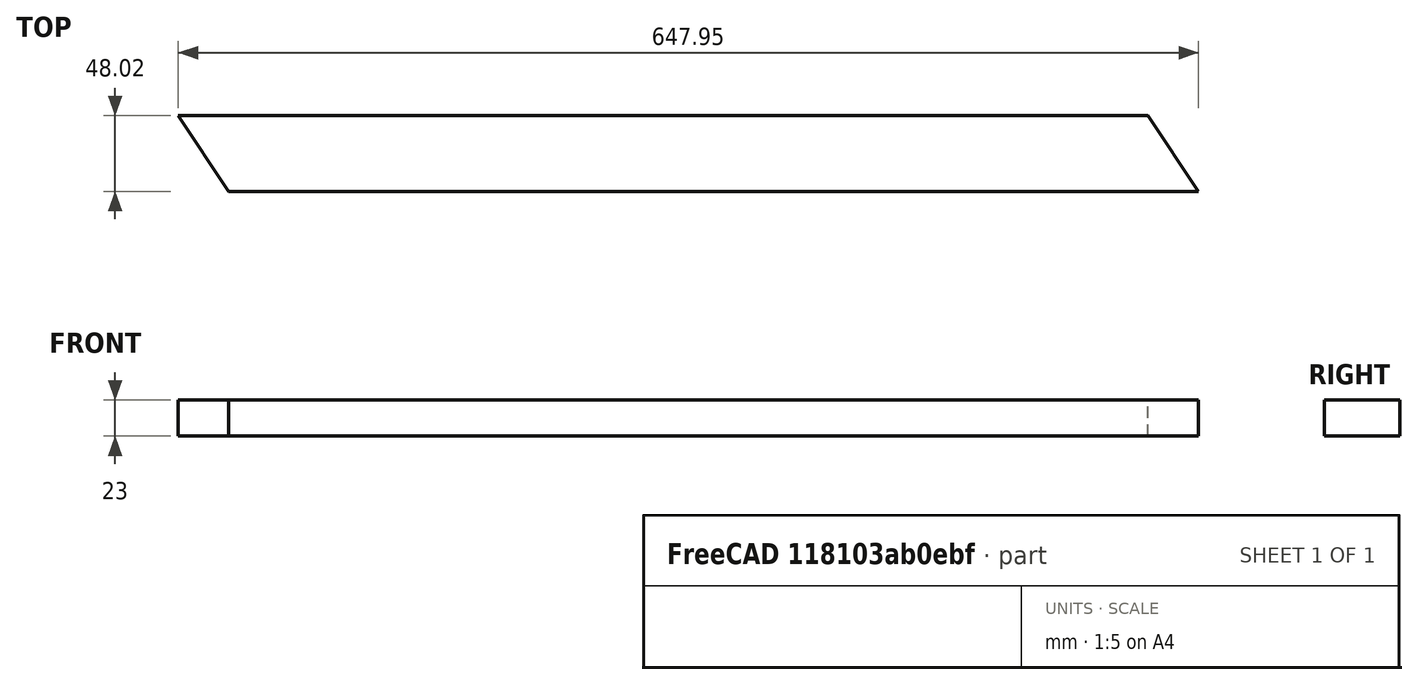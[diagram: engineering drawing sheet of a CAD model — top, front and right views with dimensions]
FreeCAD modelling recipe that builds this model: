
FCSTD DOCUMENT  (FreeCAD 0.19R24267 (Git))
Label: shelfZ
License: Creative Commons Attribution-ShareAlike
LicenseURL: http://creativecommons.org/licenses/by-sa/4.0/
objects: Sketcher::SketchObject×1, Part::Extrusion×1
note: 2 computed .brp shape members not serialized (recipe doc carries the construction recipe); baked Part::Feature solids carry a one-line shape summary decoded from their .brp
EXTERNAL_REF file=Main.FCStd obj=Spreadsheet

FEATURE [Sketcher::SketchObject] Sketch
  FullyConstrained = false
  expr: Constraints[24] = Main#<<params>>.shelfWoodWidth
  expr: Constraints[6] = Main#<<params>>.outerDeep
  expr: Constraints[2] = Main#<<params>>.outerWidth - Main#<<params>>.shelfWoodWidth * 6
  sketch-geometry (10):
    g0: LineSegment StartX=0 StartY=0 StartZ=0 EndX=512 EndY=0 EndZ=0
    g1: LineSegment StartX=0 StartY=0 StartZ=0 EndX=0 EndY=-400 EndZ=0
    g2: LineSegment StartX=0 StartY=-400 StartZ=0 EndX=512 EndY=-400 EndZ=0
    g3: LineSegment StartX=512 StartY=0 StartZ=0 EndX=512 EndY=-400 EndZ=0
    g4: LineSegment StartX=0 StartY=0 StartZ=0 EndX=512 EndY=-342.263 EndZ=0
    g5: LineSegment StartX=512 StartY=-342.263 StartZ=0 EndX=512 EndY=-400 EndZ=0
    g6: LineSegment StartX=512 StartY=-400 StartZ=0 EndX=0 EndY=-57.7372 EndZ=0
    g7: LineSegment StartX=0 StartY=-57.7372 StartZ=0 EndX=0 EndY=0 EndZ=0
    g8: LineSegment StartX=302.849 StartY=-260.186 StartZ=0 EndX=329.524 EndY=-220.281 EndZ=0
    g9: LineSegment StartX=512 StartY=-400 StartZ=0 EndX=538.676 EndY=-360.095 EndZ=0
  constraints (28):
    c: PointOnObject(g0,g-2)
    c: Horizontal(g0)
    c: Distance(g0) = 512
    c: PointOnObject(g0,g-1)
    c: Coincident(g1,g-1)
    c: PointOnObject(g1,g-2)
    c: Distance(g1) = 400
    c: Coincident(g2,g1)
    c: Horizontal(g2)
    c: Coincident(g3,g0)
    c: Vertical(g3)
    c: Coincident(g3,g2)
    c: Coincident(g4,g-1)
    c: PointOnObject(g4,g3)
    c: Coincident(g5,g4)
    c: Coincident(g5,g2)
    c: Coincident(g6,g5)
    c: PointOnObject(g6,g1)
    c: Coincident(g7,g6)
    c: Coincident(g7,g4)
    c: PointOnObject(g8,g6)
    c: PointOnObject(g8,g4)
    c: Parallel(g4,g6)
    c: Perpendicular(g6,g8)
    c: Distance(g8) = 48
    c: Coincident(g9,g5)
    c: Perpendicular(g6,g9)
    c: PointOnObject(g9,g4)
FEATURE [Part::Extrusion] Extrude
  Base = -> Sketch
  Dir = (0,0,1)
  DirMode = 2
  FaceMakerClass = Part::FaceMakerBullseye
  LengthFwd = 23
  LengthRev = 0
  Placement = pos=(0,0,0) rot=(0,0,1;0.589223rad)
  Solid = true
  Symmetric = false
  expr: LengthFwd = Main#<<params>>.shelfWoodHeight
